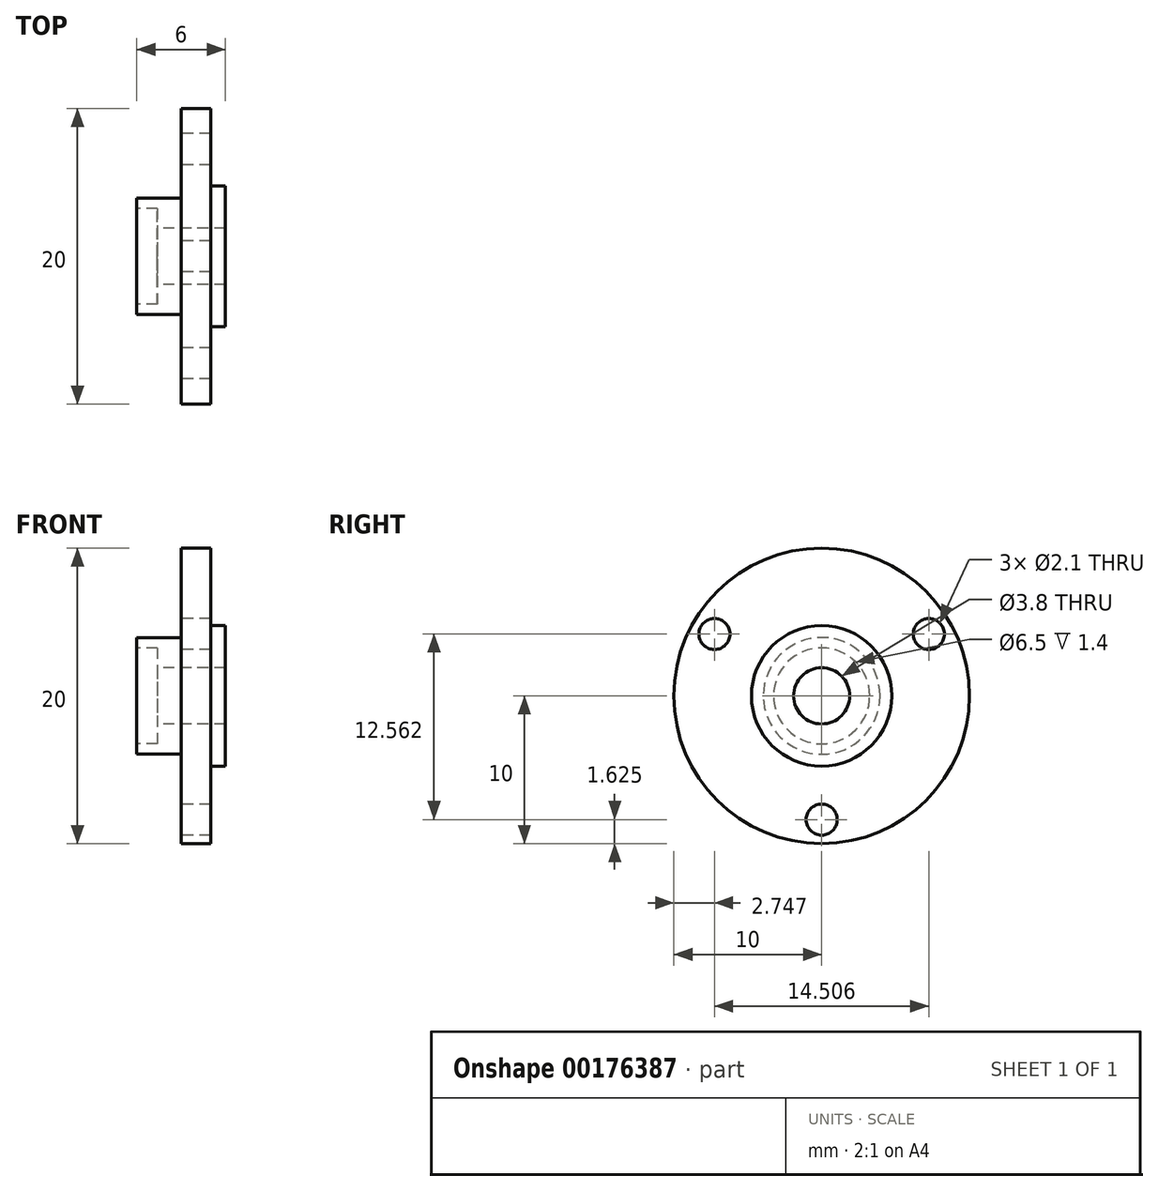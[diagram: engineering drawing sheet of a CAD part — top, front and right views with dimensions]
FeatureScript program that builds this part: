
annotation { "Feature Type Name" : "Feature", "Feature Type Description" : "" }
export const myFeature = defineFeature(function(context is Context, id is Id, definition is map)
    precondition{}
    {
        {
            var Q0;
            Q0=qCreatedBy(makeId("Front.planeOp"),FACE);
            var sketch = newSketch(context, id + "F0", { "sketchPlane" : qUnion([Q0])});
            skLineSegment(sketch, "E0", {"start": v(0, 0) * mm, "end": v(25.16, 0) * mm, "construction": true});
            skLineSegment(sketch, "E1", {"start": v(4.6, 1.9) * mm, "end": v(0, 1.9) * mm});
            skLineSegment(sketch, "E2", {"start": v(0, 1.9) * mm, "end": v(0, 3.25) * mm});
            skLineSegment(sketch, "E3", {"start": v(0, 3.25) * mm, "end": v(-1.4, 3.25) * mm});
            skLineSegment(sketch, "E4", {"start": v(-1.4, 3.25) * mm, "end": v(-1.4, 3.95) * mm});
            skLineSegment(sketch, "E5", {"start": v(-1.4, 3.95) * mm, "end": v(1.6, 3.95) * mm});
            skLineSegment(sketch, "E6", {"start": v(1.6, 3.95) * mm, "end": v(1.6, 10) * mm});
            skLineSegment(sketch, "E7", {"start": v(1.6, 10) * mm, "end": v(3.6, 10) * mm});
            skLineSegment(sketch, "E8", {"start": v(3.6, 10) * mm, "end": v(3.6, 4.75) * mm});
            skLineSegment(sketch, "E9", {"start": v(3.6, 4.75) * mm, "end": v(4.6, 4.75) * mm});
            skLineSegment(sketch, "E10", {"start": v(4.6, 4.75) * mm, "end": v(4.6, 1.9) * mm});
            skSolve(sketch);
        }
        {
            var Q0;
            Q0=makeQuery(id+"F0.imprint","IMPRINT",FACE,{"disambiguationData":[TD([[makeQuery(id+"F0.imprint","IMPRINT",EDGE,{"derivedFrom":sQuery(id+"F0.wireOp",EDGE,"E1")}),-1.0]])]});
            var Q1;
            Q1=sQuery(id+"F0.wireOp",EDGE,"E0");
            revolve(context, id + "F1", {"entities" : qUnion([Q0]), "axis" : qUnion([Q1]), "revolveType" : RevolveType.FULL});
        }
        {
            var Q0;
            Q0=makeQuery(id+"F1.opRevolve","SWEPT_FACE",FACE,{"disambiguationData":[OSD([sQuery(id+"F0.wireOp",EDGE,"E6")])]});
            var sketch = newSketch(context, id + "F2", { "sketchPlane" : qUnion([Q0])});
            skCircle(sketch, "E11", {"center": v(0, 0) * mm, "radius": 8.38 * mm, "construction": true});
            skCircle(sketch, "E12", {"center": v(-7.25, 4.19) * mm, "radius": 1.05 * mm});
            skCircle(sketch, "E13.1.0", {"center": v(0, -8.38) * mm, "radius": 1.05 * mm});
            skCircle(sketch, "E13.2.0", {"center": v(7.25, 4.19) * mm, "radius": 1.05 * mm});
            skLineSegment(sketch, "E14", {"start": v(-7.25, 4.19) * mm, "end": v(0, 0) * mm, "construction": true});
            skLineSegment(sketch, "E15", {"start": v(0, 0) * mm, "end": v(0, -8.38) * mm, "construction": true});
            skSolve(sketch);
        }
        {
            var Q0;
            Q0=makeQuery(id+"F2.imprint","IMPRINT",FACE,{"disambiguationData":[TD([[makeQuery(id+"F2.imprint","IMPRINT",EDGE,{"derivedFrom":sQuery(id+"F2.wireOp",EDGE,"E12")}),1.0]])]});
            var Q1;
            Q1=makeQuery(id+"F2.imprint","IMPRINT",FACE,{"disambiguationData":[TD([[makeQuery(id+"F2.imprint","IMPRINT",EDGE,{"derivedFrom":sQuery(id+"F2.wireOp",EDGE,"E13.2.0")}),1.0]])]});
            var Q2;
            Q2=makeQuery(id+"F2.imprint","IMPRINT",FACE,{"disambiguationData":[TD([[makeQuery(id+"F2.imprint","IMPRINT",EDGE,{"derivedFrom":sQuery(id+"F2.wireOp",EDGE,"E13.1.0")}),1.0]])]});
            extrude(context, id + "F3", {"entities" : qUnion([Q0, Q1, Q2]), "operationType" : NewBodyOperationType.REMOVE, "endBound" : BoundingType.THROUGH_ALL, "oppositeDirection" : true, "depth" : 25 * mm});
        }
    });
